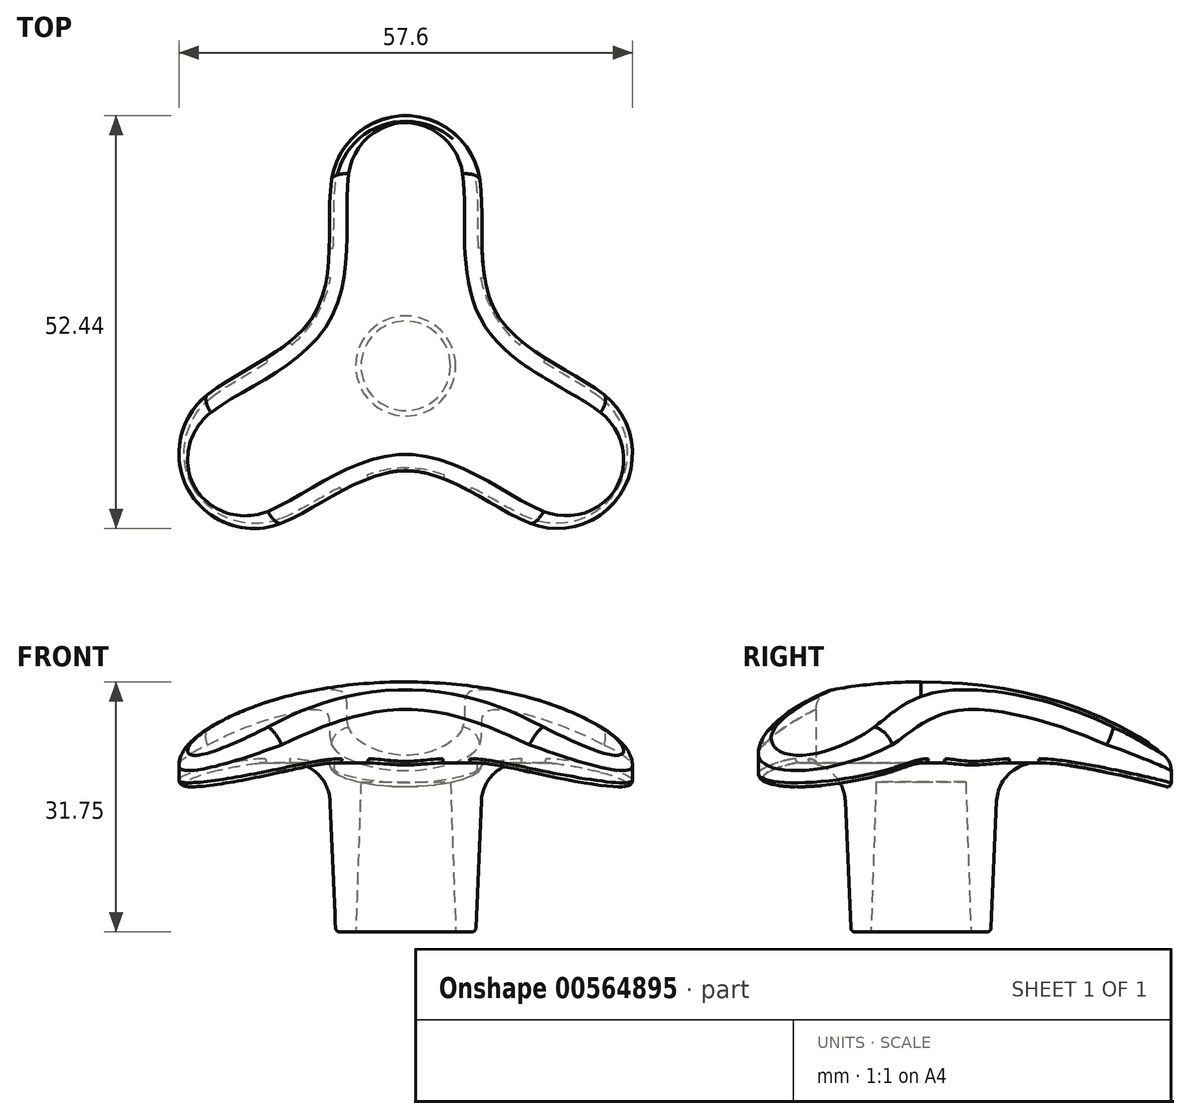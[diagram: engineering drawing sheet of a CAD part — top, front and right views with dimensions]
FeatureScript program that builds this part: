
annotation { "Feature Type Name" : "Feature", "Feature Type Description" : "" }
export const myFeature = defineFeature(function(context is Context, id is Id, definition is map)
    precondition{}
    {
        {
            var Q0;
            Q0=qCreatedBy(makeId("Top.planeOp"),FACE);
            var sketch = newSketch(context, id + "F0", { "sketchPlane" : qUnion([Q0])});
            skCircle(sketch, "E0", {"center": v(0, 0) * mm, "radius": 6.35 * mm});
            skSolve(sketch);
        }
        {
            var Q0;
            Q0=qCreatedBy(makeId("Front.planeOp"),FACE);
            var sketch = newSketch(context, id + "F1", { "sketchPlane" : qUnion([Q0])});
            skLineSegment(sketch, "E1", {"start": v(6.35, 0) * mm, "end": v(6.35, -19.05) * mm, "construction": true});
            skLineSegment(sketch, "E2", {"start": v(6.35, 0) * mm, "end": v(0, 0) * mm, "construction": true});
            skLineSegment(sketch, "E3", {"start": v(6.35, -19.05) * mm, "end": v(5.68, 0) * mm});
            skLineSegment(sketch, "E4", {"start": v(5.68, 0) * mm, "end": v(0, 0) * mm});
            skLineSegment(sketch, "E5", {"start": v(6.35, -19.05) * mm, "end": v(8.4, -19.05) * mm});
            skLineSegment(sketch, "E6", {"start": v(0, 0) * mm, "end": v(0, 12.7) * mm});
            skFitSpline(sketch, "E7", {"points": [v(0, 12.7) * mm, v(33.02, 0.91) * mm, v(33.02, -1.63) * mm], "startDerivative": vector(76.46, 0) * mm, "endDerivative": vector(1.17, -20.01) * mm});
            skLineSegment(sketch, "E8", {"start": v(33.02, -1.63) * mm, "end": v(33.02, 0.91) * mm});
            skLineSegment(sketch, "E9", {"start": v(8.91, -18.56) * mm, "end": v(9.61, -2.43) * mm});
            skLineSegment(sketch, "E10", {"start": v(14.69, 2.43) * mm, "end": v(17.55, 2.43) * mm});
            skFitSpline(sketch, "E11", {"points": [v(17.55, 2.43) * mm, v(33.02, -1.63) * mm], "startDerivative": vector(11.14, 0) * mm, "endDerivative": vector(5.43, -4.88) * mm});
            skPoint(sketch, "E12.visualSharp", {"position": v(9.82, 2.43) * mm});
            skArc(sketch, "E12.filletArc", {"start": v(14.69, 2.43) * mm, "mid": v(11.17, 1.02) * mm, "end": v(9.61, -2.43) * mm});
            skPoint(sketch, "E13.visualSharp", {"position": v(8.9, -19.05) * mm});
            skArc(sketch, "E13.filletArc", {"start": v(8.4, -19.05) * mm, "mid": v(8.75, -18.9) * mm, "end": v(8.91, -18.56) * mm});
            skLineSegment(sketch, "E14", {"start": v(17.55, 2.43) * mm, "end": v(21.27, 2.43) * mm, "construction": true});
            skSolve(sketch);
        }
        {
            var Q0;
            Q0 = qSketchRegion(id + "F1", true);
            var Q1;
            Q1=sQuery(id+"F1.wireOp",EDGE,"E6");
            revolve(context, id + "F2", {"entities" : qUnion([Q0]), "axis" : qUnion([Q1]), "revolveType" : RevolveType.FULL});
        }
        {
            var Q0;
            Q0=qCreatedBy(makeId("Top.planeOp"),FACE);
            var sketch = newSketch(context, id + "F3", { "sketchPlane" : qUnion([Q0])});
            skCircle(sketch, "E15", {"center": v(0, 0) * mm, "radius": 38.1 * mm});
            skLineSegment(sketch, "E16", {"start": v(0, 0) * mm, "end": v(0, 38.1) * mm, "construction": true});
            skLineSegment(sketch, "E17", {"start": v(0, 0) * mm, "end": v(-33, -19.05) * mm, "construction": true});
            skLineSegment(sketch, "E18", {"start": v(0, 0) * mm, "end": v(33, -19.05) * mm, "construction": true});
            skCircle(sketch, "E19", {"center": v(0, 0) * mm, "radius": 31.75 * mm, "construction": true});
            skCircle(sketch, "E20", {"center": v(0, 22.23) * mm, "radius": 9.53 * mm});
            skCircle(sketch, "E21.1.0", {"center": v(-19.25, -11.11) * mm, "radius": 9.53 * mm, "construction": true});
            skCircle(sketch, "E21.2.0", {"center": v(19.25, -11.11) * mm, "radius": 9.53 * mm, "construction": true});
            skLineSegment(sketch, "E22", {"start": v(0, 0) * mm, "end": v(-33, 19.05) * mm, "construction": true});
            skFitSpline(sketch, "E23", {"points": [v(-9.42, 23.64) * mm, v(-11.54, 6.66) * mm, v(-25.18, -3.66) * mm], "startDerivative": vector(-4.39, -29.16) * mm, "endDerivative": vector(-23.06, -18.33) * mm});
            skFitSpline(sketch, "E24.MirrorCS", {"points": [v(15.77, -19.98) * mm, v(0, -13.32) * mm, v(-15.75, -19.97) * mm], "startDerivative": vector(-27.45, 10.78) * mm, "endDerivative": vector(-27.4, -10.8) * mm});
            skFitSpline(sketch, "E25.MirrorCS", {"points": [v(25.18, -3.66) * mm, v(11.54, 6.66) * mm, v(9.42, 23.63) * mm], "startDerivative": vector(-23.06, 18.38) * mm, "endDerivative": vector(-4.35, 29.13) * mm});
            skArc(sketch, "E26", {"start": v(9.42, 23.63) * mm, "mid": v(0, 31.79) * mm, "end": v(-9.42, 23.64) * mm});
            skPoint(sketch, "E27", {"position": v(0, 31.75) * mm});
            skArc(sketch, "E28.MirrorCS", {"start": v(-15.75, -19.97) * mm, "mid": v(-27.53, -15.9) * mm, "end": v(-25.18, -3.66) * mm});
            skArc(sketch, "E29.1.0", {"start": v(-25.18, -3.66) * mm, "mid": v(-27.53, -15.89) * mm, "end": v(-15.77, -19.98) * mm});
            skArc(sketch, "E29.2.0", {"start": v(15.75, -19.97) * mm, "mid": v(27.53, -15.9) * mm, "end": v(25.18, -3.66) * mm});
            skSolve(sketch);
        }
        {
            var Q0;
            Q0 = qSketchRegion(id + "F3", true);
            extrude(context, id + "F4", {"entities" : qUnion([Q0]), "operationType" : NewBodyOperationType.REMOVE, "endBound" : BoundingType.SYMMETRIC, "depth" : 25.4 * mm, "offsetDistance" : 25.4 * mm});
        }
        {
            var Q0;
            Q0=makeQuery(id+"F2.opRevolve","SWEPT_FACE",FACE,{"disambiguationData":[OSD([sQuery(id+"F1.wireOp",EDGE,"E7")])]});
            fillet(context, id + "F5", {"entities" : qUnion([Q0]), "radius" : 2.54 * mm, "tangentPropagation" : true, "allowEdgeOverflow" : false});
        }
        {
            var Q0;
            Q0=makeQuery(id+"F4.boolean.opBoolean","INTERSECT",EDGE,{"disambiguationData":[OD(0.0)],"derivedFrom":[makeQuery(id+"F2.opRevolve","SWEPT_FACE",FACE,{"disambiguationData":[OSD([sQuery(id+"F1.wireOp",EDGE,"E11")])]}),makeQuery(id+"F4.opExtrude","SWEPT_FACE",FACE,{"disambiguationData":[OSD([sQuery(id+"F3.wireOp",EDGE,"E25.MirrorCS")])]})]});
            var Q1;
            Q1=makeQuery(id+"F4.boolean.opBoolean","INTERSECT",EDGE,{"derivedFrom":[makeQuery(id+"F2.opRevolve","SWEPT_FACE",FACE,{"disambiguationData":[OSD([sQuery(id+"F1.wireOp",EDGE,"E11")])]}),makeQuery(id+"F4.opExtrude","SWEPT_FACE",FACE,{"disambiguationData":[OSD([sQuery(id+"F3.wireOp",EDGE,"E29.2.0")])]})]});
            var Q2;
            Q2=makeQuery(id+"F4.boolean.opBoolean","INTERSECT",EDGE,{"disambiguationData":[OD(1.0)],"derivedFrom":[makeQuery(id+"F2.opRevolve","SWEPT_FACE",FACE,{"disambiguationData":[OSD([sQuery(id+"F1.wireOp",EDGE,"E10")])]}),makeQuery(id+"F4.opExtrude","SWEPT_FACE",FACE,{"disambiguationData":[OSD([sQuery(id+"F3.wireOp",EDGE,"E25.MirrorCS")])]})]});
            var Q3;
            Q3=makeQuery(id+"F4.boolean.opBoolean","INTERSECT",EDGE,{"derivedFrom":[makeQuery(id+"F2.opRevolve","SWEPT_FACE",FACE,{"disambiguationData":[OSD([sQuery(id+"F1.wireOp",EDGE,"E12.filletArc")])]}),makeQuery(id+"F4.opExtrude","SWEPT_FACE",FACE,{"disambiguationData":[OSD([sQuery(id+"F3.wireOp",EDGE,"E25.MirrorCS")])]})]});
            var Q4;
            Q4=makeQuery(id+"F4.boolean.opBoolean","INTERSECT",EDGE,{"disambiguationData":[OD(0.0)],"derivedFrom":[makeQuery(id+"F2.opRevolve","SWEPT_FACE",FACE,{"disambiguationData":[OSD([sQuery(id+"F1.wireOp",EDGE,"E10")])]}),makeQuery(id+"F4.opExtrude","SWEPT_FACE",FACE,{"disambiguationData":[OSD([sQuery(id+"F3.wireOp",EDGE,"E25.MirrorCS")])]})]});
            var Q5;
            Q5=makeQuery(id+"F4.boolean.opBoolean","INTERSECT",EDGE,{"disambiguationData":[OD(1.0)],"derivedFrom":[makeQuery(id+"F2.opRevolve","SWEPT_FACE",FACE,{"disambiguationData":[OSD([sQuery(id+"F1.wireOp",EDGE,"E11")])]}),makeQuery(id+"F4.opExtrude","SWEPT_FACE",FACE,{"disambiguationData":[OSD([sQuery(id+"F3.wireOp",EDGE,"E25.MirrorCS")])]})]});
            var Q6;
            Q6=makeQuery(id+"F4.boolean.opBoolean","INTERSECT",EDGE,{"derivedFrom":[makeQuery(id+"F2.opRevolve","SWEPT_FACE",FACE,{"disambiguationData":[OSD([sQuery(id+"F1.wireOp",EDGE,"E11")])]}),makeQuery(id+"F4.opExtrude","SWEPT_FACE",FACE,{"disambiguationData":[OSD([sQuery(id+"F3.wireOp",EDGE,"E26")])]})]});
            var Q7;
            Q7=makeQuery(id+"F4.boolean.opBoolean","INTERSECT",EDGE,{"disambiguationData":[OD(0.0)],"derivedFrom":[makeQuery(id+"F2.opRevolve","SWEPT_FACE",FACE,{"disambiguationData":[OSD([sQuery(id+"F1.wireOp",EDGE,"E11")])]}),makeQuery(id+"F4.opExtrude","SWEPT_FACE",FACE,{"disambiguationData":[OSD([sQuery(id+"F3.wireOp",EDGE,"E23")])]})]});
            var Q8;
            Q8=makeQuery(id+"F4.boolean.opBoolean","INTERSECT",EDGE,{"disambiguationData":[OD(1.0)],"derivedFrom":[makeQuery(id+"F2.opRevolve","SWEPT_FACE",FACE,{"disambiguationData":[OSD([sQuery(id+"F1.wireOp",EDGE,"E10")])]}),makeQuery(id+"F4.opExtrude","SWEPT_FACE",FACE,{"disambiguationData":[OSD([sQuery(id+"F3.wireOp",EDGE,"E23")])]})]});
            var Q9;
            Q9=makeQuery(id+"F4.boolean.opBoolean","INTERSECT",EDGE,{"derivedFrom":[makeQuery(id+"F2.opRevolve","SWEPT_FACE",FACE,{"disambiguationData":[OSD([sQuery(id+"F1.wireOp",EDGE,"E12.filletArc")])]}),makeQuery(id+"F4.opExtrude","SWEPT_FACE",FACE,{"disambiguationData":[OSD([sQuery(id+"F3.wireOp",EDGE,"E23")])]})]});
            var Q10;
            Q10=makeQuery(id+"F4.boolean.opBoolean","INTERSECT",EDGE,{"disambiguationData":[OD(0.0)],"derivedFrom":[makeQuery(id+"F2.opRevolve","SWEPT_FACE",FACE,{"disambiguationData":[OSD([sQuery(id+"F1.wireOp",EDGE,"E11")])]}),makeQuery(id+"F4.opExtrude","SWEPT_FACE",FACE,{"disambiguationData":[OSD([sQuery(id+"F3.wireOp",EDGE,"E24.MirrorCS")])]})]});
            var Q11;
            Q11=makeQuery(id+"F4.boolean.opBoolean","INTERSECT",EDGE,{"disambiguationData":[OD(1.0)],"derivedFrom":[makeQuery(id+"F2.opRevolve","SWEPT_FACE",FACE,{"disambiguationData":[OSD([sQuery(id+"F1.wireOp",EDGE,"E10")])]}),makeQuery(id+"F4.opExtrude","SWEPT_FACE",FACE,{"disambiguationData":[OSD([sQuery(id+"F3.wireOp",EDGE,"E24.MirrorCS")])]})]});
            var Q12;
            Q12=makeQuery(id+"F4.boolean.opBoolean","INTERSECT",EDGE,{"derivedFrom":[makeQuery(id+"F2.opRevolve","SWEPT_FACE",FACE,{"disambiguationData":[OSD([sQuery(id+"F1.wireOp",EDGE,"E12.filletArc")])]}),makeQuery(id+"F4.opExtrude","SWEPT_FACE",FACE,{"disambiguationData":[OSD([sQuery(id+"F3.wireOp",EDGE,"E24.MirrorCS")])]})]});
            var Q13;
            Q13=makeQuery(id+"F4.boolean.opBoolean","INTERSECT",EDGE,{"disambiguationData":[OD(0.0)],"derivedFrom":[makeQuery(id+"F2.opRevolve","SWEPT_FACE",FACE,{"disambiguationData":[OSD([sQuery(id+"F1.wireOp",EDGE,"E10")])]}),makeQuery(id+"F4.opExtrude","SWEPT_FACE",FACE,{"disambiguationData":[OSD([sQuery(id+"F3.wireOp",EDGE,"E24.MirrorCS")])]})]});
            var Q14;
            Q14=makeQuery(id+"F4.boolean.opBoolean","INTERSECT",EDGE,{"disambiguationData":[OD(1.0)],"derivedFrom":[makeQuery(id+"F2.opRevolve","SWEPT_FACE",FACE,{"disambiguationData":[OSD([sQuery(id+"F1.wireOp",EDGE,"E11")])]}),makeQuery(id+"F4.opExtrude","SWEPT_FACE",FACE,{"disambiguationData":[OSD([sQuery(id+"F3.wireOp",EDGE,"E24.MirrorCS")])]})]});
            var Q15;
            Q15=makeQuery(id+"F4.boolean.opBoolean","INTERSECT",EDGE,{"derivedFrom":[makeQuery(id+"F2.opRevolve","SWEPT_FACE",FACE,{"disambiguationData":[OSD([sQuery(id+"F1.wireOp",EDGE,"E11")])]}),makeQuery(id+"F4.opExtrude","SWEPT_FACE",FACE,{"disambiguationData":[OSD([sQuery(id+"F3.wireOp",EDGE,"E29.1.0")])]})]});
            var Q16;
            Q16=makeQuery(id+"F4.boolean.opBoolean","INTERSECT",EDGE,{"disambiguationData":[OD(0.0)],"derivedFrom":[makeQuery(id+"F2.opRevolve","SWEPT_FACE",FACE,{"disambiguationData":[OSD([sQuery(id+"F1.wireOp",EDGE,"E10")])]}),makeQuery(id+"F4.opExtrude","SWEPT_FACE",FACE,{"disambiguationData":[OSD([sQuery(id+"F3.wireOp",EDGE,"E23")])]})]});
            var Q17;
            Q17=makeQuery(id+"F4.boolean.opBoolean","INTERSECT",EDGE,{"disambiguationData":[OD(1.0)],"derivedFrom":[makeQuery(id+"F2.opRevolve","SWEPT_FACE",FACE,{"disambiguationData":[OSD([sQuery(id+"F1.wireOp",EDGE,"E11")])]}),makeQuery(id+"F4.opExtrude","SWEPT_FACE",FACE,{"disambiguationData":[OSD([sQuery(id+"F3.wireOp",EDGE,"E23")])]})]});
            fillet(context, id + "F6", {"entities" : qUnion([Q0, Q1, Q2, Q3, Q4, Q5, Q6, Q7, Q8, Q9, Q10, Q11, Q12, Q13, Q14, Q15, Q16, Q17]), "radius" : 0.5 * mm, "tangentPropagation" : true, "allowEdgeOverflow" : false});
        }
    });
